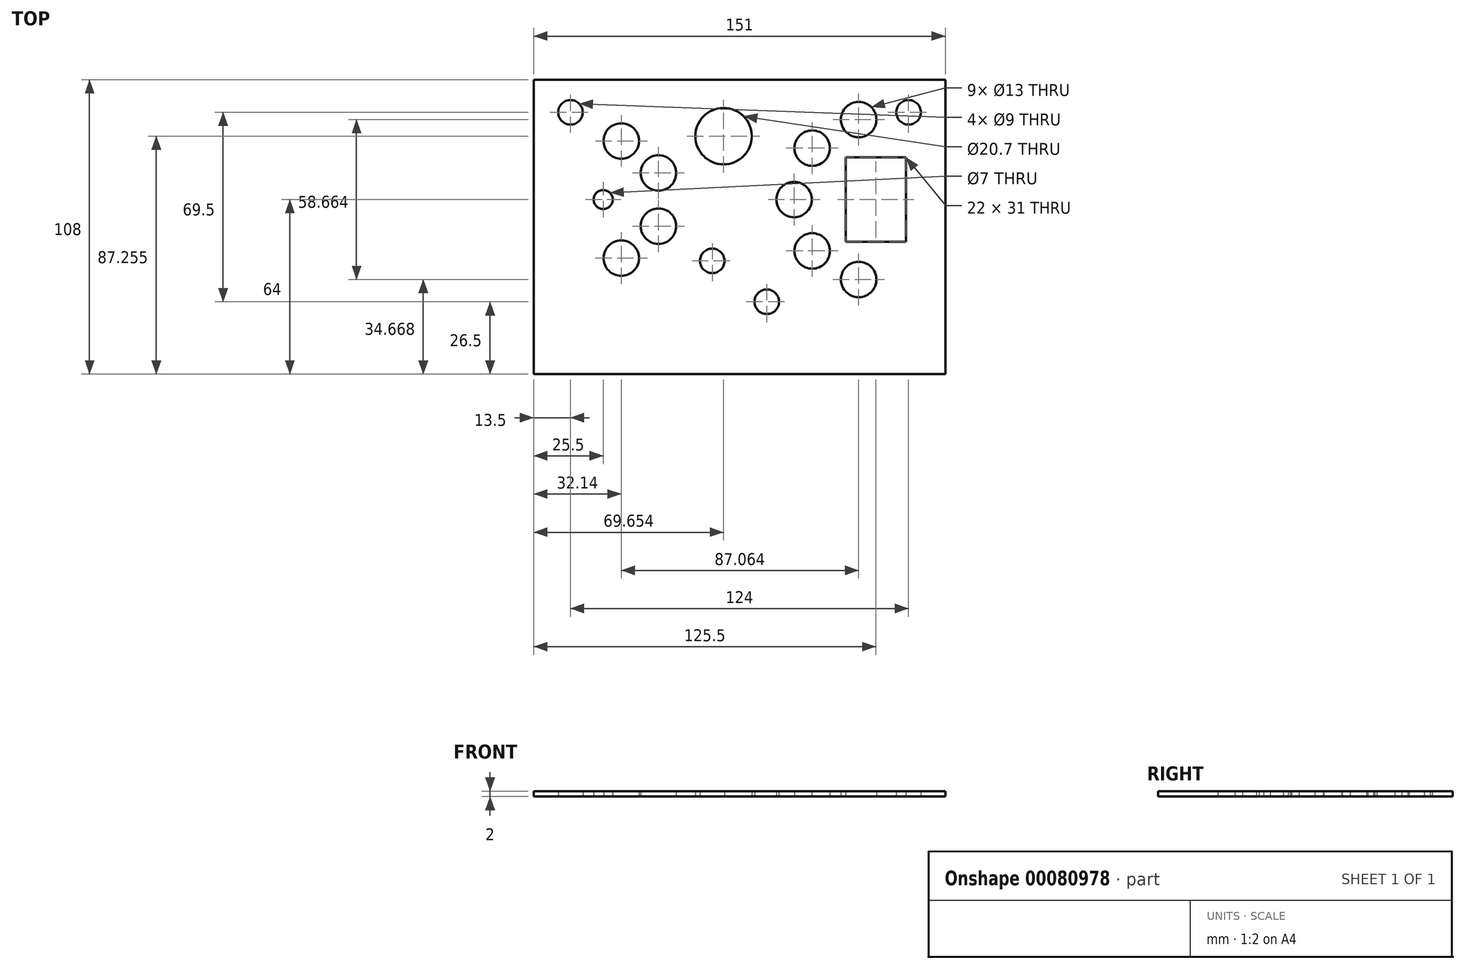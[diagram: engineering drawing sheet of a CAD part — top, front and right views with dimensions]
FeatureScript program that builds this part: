
annotation { "Feature Type Name" : "Feature", "Feature Type Description" : "" }
export const myFeature = defineFeature(function(context is Context, id is Id, definition is map)
    precondition{}
    {
        {
            var Q0;
            Q0=qCreatedBy(makeId("Top.planeOp"),FACE);
            var sketch = newSketch(context, id + "F0", { "sketchPlane" : qUnion([Q0])});
            skPoint(sketch, "E0.middle", {"position": v(0, 0) * mm});
            skPoint(sketch, "E1.visualSharp", {"position": v(-70, 50) * mm});
            skPoint(sketch, "E2.visualSharp", {"position": v(-70, -50) * mm});
            skPoint(sketch, "E3.visualSharp", {"position": v(70, -50) * mm});
            skPoint(sketch, "E4.visualSharp", {"position": v(70, 50) * mm});
            skPoint(sketch, "E5", {"position": v(-5.85, 33.26) * mm});
            skCircle(sketch, "E6", {"center": v(-5.85, 33.26) * mm, "radius": 10.35 * mm});
            skLineSegment(sketch, "E7.bottom", {"start": v(-10, -12.5) * mm, "end": v(10, -12.5) * mm, "construction": true});
            skLineSegment(sketch, "E7.top", {"start": v(-10, -27.5) * mm, "end": v(10, -27.5) * mm, "construction": true});
            skLineSegment(sketch, "E7.left", {"start": v(-10, -12.5) * mm, "end": v(-10, -27.5) * mm, "construction": true});
            skLineSegment(sketch, "E7.right", {"start": v(10, -12.5) * mm, "end": v(10, -27.5) * mm, "construction": true});
            skPoint(sketch, "E7.middle", {"position": v(0, -20) * mm});
            skLineSegment(sketch, "E8", {"start": v(0, -20) * mm, "end": v(0, 0) * mm, "construction": true});
            skCircle(sketch, "E9.MirrorC", {"center": v(-50, 10) * mm, "radius": 15 * mm, "construction": true});
            skCircle(sketch, "E10.MirrorC", {"center": v(-50, 10) * mm, "radius": 3.5 * mm});
            skPoint(sketch, "E11.MirrorP", {"position": v(50, 10) * mm});
            skCircle(sketch, "E12", {"center": v(-50, 10) * mm, "radius": 22.5 * mm, "construction": true});
            skPoint(sketch, "E13", {"position": v(-27.5, 10) * mm});
            skCircle(sketch, "E14", {"center": v(-29.72, 19.75) * mm, "radius": 6.5 * mm});
            skCircle(sketch, "E15", {"center": v(-43.36, 31.5) * mm, "radius": 6.5 * mm});
            skCircle(sketch, "E16", {"center": v(-62, 42) * mm, "radius": 4.5 * mm});
            skCircle(sketch, "E17", {"center": v(62, 42) * mm, "radius": 4.5 * mm});
            skLineSegment(sketch, "E18.bottom", {"start": v(39, 25.5) * mm, "end": v(61, 25.5) * mm});
            skLineSegment(sketch, "E18.top", {"start": v(39, -5.5) * mm, "end": v(61, -5.5) * mm});
            skLineSegment(sketch, "E18.left", {"start": v(39, 25.5) * mm, "end": v(39, -5.5) * mm});
            skLineSegment(sketch, "E18.right", {"start": v(61, 25.5) * mm, "end": v(61, -5.5) * mm});
            skLineSegment(sketch, "E19", {"start": v(50, 10) * mm, "end": v(0, 10) * mm, "construction": true});
            skLineSegment(sketch, "E20", {"start": v(0, 10) * mm, "end": v(0, 0) * mm, "construction": true});
            skCircle(sketch, "E21", {"center": v(50, 10) * mm, "radius": 30 * mm, "construction": true});
            skCircle(sketch, "E22", {"center": v(20, 10) * mm, "radius": 6.5 * mm});
            skCircle(sketch, "E23", {"center": v(-29.72, 0.25) * mm, "radius": 6.5 * mm});
            skCircle(sketch, "E24", {"center": v(-43.36, -11.5) * mm, "radius": 6.5 * mm});
            skLineSegment(sketch, "E25", {"start": v(-43.36, -11.5) * mm, "end": v(-29.72, 0.25) * mm, "construction": true});
            skLineSegment(sketch, "E26", {"start": v(-29.72, 0.25) * mm, "end": v(-27.5, 10) * mm, "construction": true});
            skLineSegment(sketch, "E27", {"start": v(-27.5, 10) * mm, "end": v(-29.72, 19.75) * mm, "construction": true});
            skLineSegment(sketch, "E28", {"start": v(-29.72, 19.75) * mm, "end": v(-43.36, 31.5) * mm, "construction": true});
            skLineSegment(sketch, "E29.bottom", {"start": v(0, 0) * mm, "end": v(-50, 0) * mm, "construction": true});
            skLineSegment(sketch, "E29.top", {"start": v(0, 10) * mm, "end": v(-50, 10) * mm, "construction": true});
            skLineSegment(sketch, "E29.left", {"start": v(0, 0) * mm, "end": v(0, 10) * mm, "construction": true});
            skLineSegment(sketch, "E29.right", {"start": v(-50, 0) * mm, "end": v(-50, 10) * mm, "construction": true});
            skCircle(sketch, "E30", {"center": v(26.67, 28.86) * mm, "radius": 6.5 * mm});
            skCircle(sketch, "E31", {"center": v(43.7, 39.33) * mm, "radius": 6.5 * mm});
            skCircle(sketch, "E32", {"center": v(26.67, -8.86) * mm, "radius": 6.5 * mm});
            skLineSegment(sketch, "E33", {"start": v(20, 10) * mm, "end": v(26.67, 28.86) * mm});
            skLineSegment(sketch, "E34", {"start": v(43.7, 39.33) * mm, "end": v(26.67, 28.86) * mm});
            skCircle(sketch, "E35", {"center": v(43.7, -19.33) * mm, "radius": 6.5 * mm});
            skLineSegment(sketch, "E36", {"start": v(43.7, -19.33) * mm, "end": v(26.67, -8.86) * mm});
            skLineSegment(sketch, "E37", {"start": v(26.67, -8.86) * mm, "end": v(20, 10) * mm});
            skLineSegment(sketch, "E38.bottom", {"start": v(-70, 50) * mm, "end": v(-62, 50) * mm, "construction": true});
            skLineSegment(sketch, "E38.top", {"start": v(-70, 42) * mm, "end": v(-62, 42) * mm, "construction": true});
            skLineSegment(sketch, "E38.left", {"start": v(-70, 50) * mm, "end": v(-70, 42) * mm, "construction": true});
            skLineSegment(sketch, "E38.right", {"start": v(-62, 50) * mm, "end": v(-62, 42) * mm, "construction": true});
            skLineSegment(sketch, "E39.bottom", {"start": v(70, 50) * mm, "end": v(62, 50) * mm, "construction": true});
            skLineSegment(sketch, "E39.top", {"start": v(70, 42) * mm, "end": v(62, 42) * mm, "construction": true});
            skLineSegment(sketch, "E39.left", {"start": v(70, 50) * mm, "end": v(70, 42) * mm, "construction": true});
            skLineSegment(sketch, "E39.right", {"start": v(62, 50) * mm, "end": v(62, 42) * mm, "construction": true});
            skCircle(sketch, "E40", {"center": v(-10, -12.5) * mm, "radius": 4.5 * mm});
            skCircle(sketch, "E41", {"center": v(10, -27.5) * mm, "radius": 4.5 * mm});
            skLineSegment(sketch, "E42.bottom", {"start": v(-75.5, 54) * mm, "end": v(75.5, 54) * mm});
            skLineSegment(sketch, "E42.top", {"start": v(-75.5, -54) * mm, "end": v(75.5, -54) * mm});
            skLineSegment(sketch, "E42.left", {"start": v(-75.5, 54) * mm, "end": v(-75.5, -54) * mm});
            skLineSegment(sketch, "E42.right", {"start": v(75.5, 54) * mm, "end": v(75.5, -54) * mm});
            skSolve(sketch);
        }
        {
            var Q0;
            Q0=qSketchRegion(id+"F0",true);
            extrude(context, id + "F1", {"entities" : qUnion([Q0]), "depth" : 2 * mm});
        }
    });
